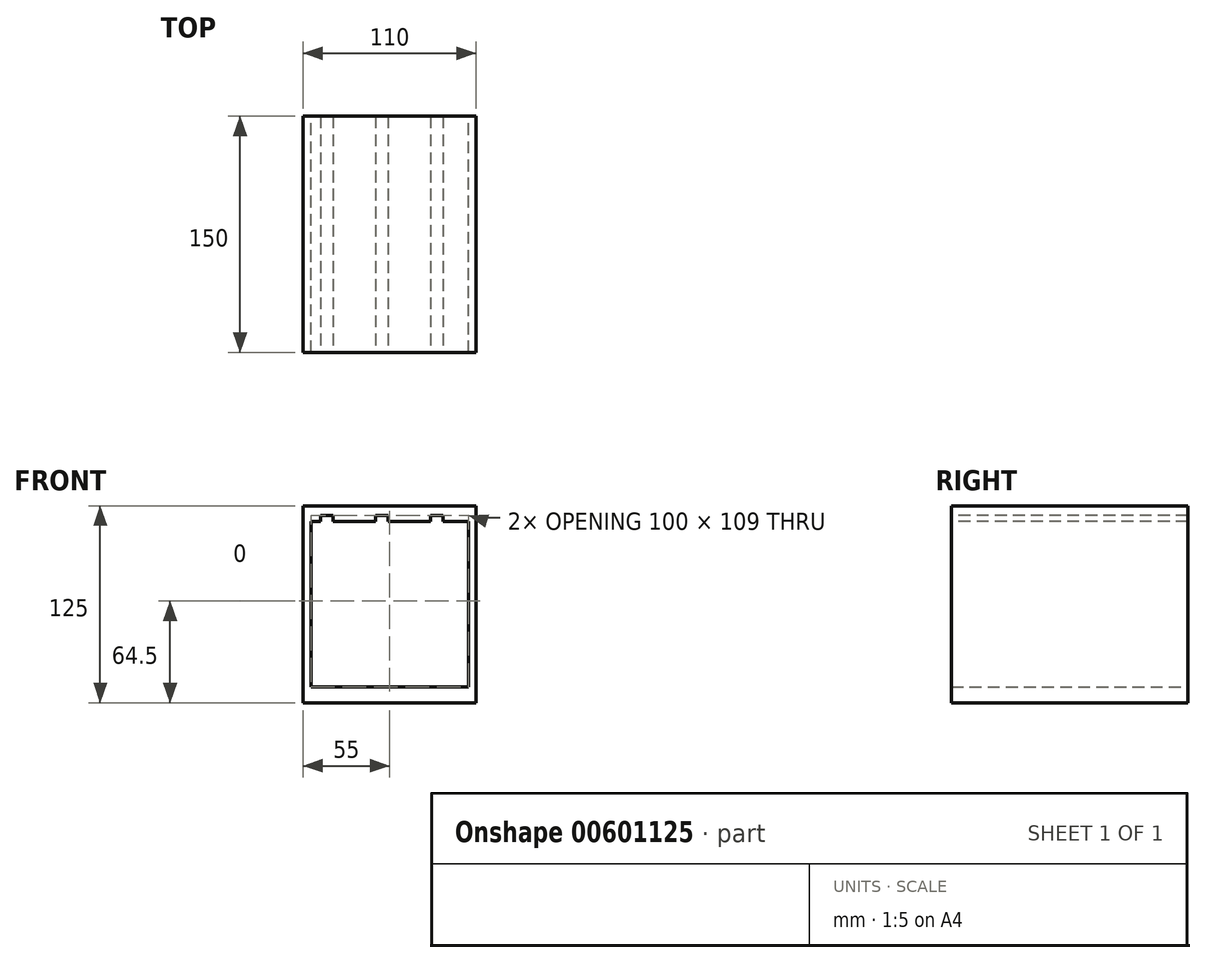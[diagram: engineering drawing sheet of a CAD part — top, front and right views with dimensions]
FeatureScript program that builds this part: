
annotation { "Feature Type Name" : "Feature", "Feature Type Description" : "" }
export const myFeature = defineFeature(function(context is Context, id is Id, definition is map)
    precondition{}
    {
        {
            var Q0;
            Q0=qCreatedBy(makeId("Front.planeOp"),FACE);
            var sketch = newSketch(context, id + "F0", { "sketchPlane" : qUnion([Q0])});
            skLineSegment(sketch, "E0.bottom", {"start": v(-50, 52.5) * mm, "end": v(50, 52.5) * mm});
            skLineSegment(sketch, "E0.top", {"start": v(-50, -52.5) * mm, "end": v(50, -52.5) * mm});
            skLineSegment(sketch, "E0.left", {"start": v(-50, 52.5) * mm, "end": v(-50, -52.5) * mm});
            skLineSegment(sketch, "E0.right", {"start": v(50, 52.5) * mm, "end": v(50, -52.5) * mm});
            skPoint(sketch, "E0.middle", {"position": v(0, 0) * mm});
            skLineSegment(sketch, "E1.bottom", {"start": v(55, -62.5) * mm, "end": v(-55, -62.5) * mm});
            skLineSegment(sketch, "E1.top", {"start": v(55, 62.5) * mm, "end": v(-55, 62.5) * mm});
            skLineSegment(sketch, "E1.left", {"start": v(55, -62.5) * mm, "end": v(55, 62.5) * mm});
            skLineSegment(sketch, "E1.right", {"start": v(-55, -62.5) * mm, "end": v(-55, 62.5) * mm});
            skSolve(sketch);
        }
        {
            var Q0;
            Q0 = qSketchRegion(id + "F0", true);
            extrude(context, id + "F1", {"entities" : qUnion([Q0]), "depth" : 150 * mm, "offsetDistance" : 25 * mm});
        }
        {
            var Q0;
            Q0=makeQuery(id+"F1.opExtrude","CAP_FACE",FACE,{"disambiguationData":[OSD([sQuery(id+"F0.wireOp",EDGE,"E0.bottom"),sQuery(id+"F0.wireOp",EDGE,"E0.top"),sQuery(id+"F0.wireOp",EDGE,"E0.left"),sQuery(id+"F0.wireOp",EDGE,"E0.right"),sQuery(id+"F0.wireOp",EDGE,"E1.bottom"),sQuery(id+"F0.wireOp",EDGE,"E1.top"),sQuery(id+"F0.wireOp",EDGE,"E1.left"),sQuery(id+"F0.wireOp",EDGE,"E1.right")])],"isStart":false});
            var sketch = newSketch(context, id + "F2", { "sketchPlane" : qUnion([Q0])});
            skLineSegment(sketch, "E2.bottom", {"start": v(-44, 52.5) * mm, "end": v(-36, 52.5) * mm});
            skLineSegment(sketch, "E2.top", {"start": v(-44, 56.5) * mm, "end": v(-36, 56.5) * mm});
            skLineSegment(sketch, "E2.left", {"start": v(-44, 52.5) * mm, "end": v(-44, 56.5) * mm});
            skLineSegment(sketch, "E2.right", {"start": v(-36, 52.5) * mm, "end": v(-36, 56.5) * mm});
            skLineSegment(sketch, "E3", {"start": v(-40, 56.5) * mm, "end": v(-40, 52.5) * mm});
            skLineSegment(sketch, "E4.1.0.0", {"start": v(-5, 56.5) * mm, "end": v(-5, 52.5) * mm});
            skLineSegment(sketch, "E4.1.0.1", {"start": v(-1, 52.5) * mm, "end": v(-1, 56.5) * mm});
            skLineSegment(sketch, "E4.1.0.2", {"start": v(-9, 52.5) * mm, "end": v(-9, 56.5) * mm});
            skLineSegment(sketch, "E4.1.0.3", {"start": v(-9, 56.5) * mm, "end": v(-1, 56.5) * mm});
            skLineSegment(sketch, "E4.1.0.4", {"start": v(-9, 52.5) * mm, "end": v(-1, 52.5) * mm});
            skLineSegment(sketch, "E4.2.0.0", {"start": v(30, 56.5) * mm, "end": v(30, 52.5) * mm});
            skLineSegment(sketch, "E4.2.0.1", {"start": v(34, 52.5) * mm, "end": v(34, 56.5) * mm});
            skLineSegment(sketch, "E4.2.0.2", {"start": v(26, 52.5) * mm, "end": v(26, 56.5) * mm});
            skLineSegment(sketch, "E4.2.0.3", {"start": v(26, 56.5) * mm, "end": v(34, 56.5) * mm});
            skLineSegment(sketch, "E4.2.0.4", {"start": v(26, 52.5) * mm, "end": v(34, 52.5) * mm});
            skLineSegment(sketch, "E4.direction1", {"start": v(-40, 52.5) * mm, "end": v(-5, 52.5) * mm, "construction": true});
            skSolve(sketch);
        }
        {
            var Q0;
            Q0 = qSketchRegion(id + "F2", true);
            extrude(context, id + "F3", {"entities" : qUnion([Q0]), "operationType" : NewBodyOperationType.REMOVE, "endBound" : BoundingType.UP_TO_NEXT, "oppositeDirection" : true, "depth" : 25 * mm, "offsetDistance" : 25 * mm});
        }
    });
